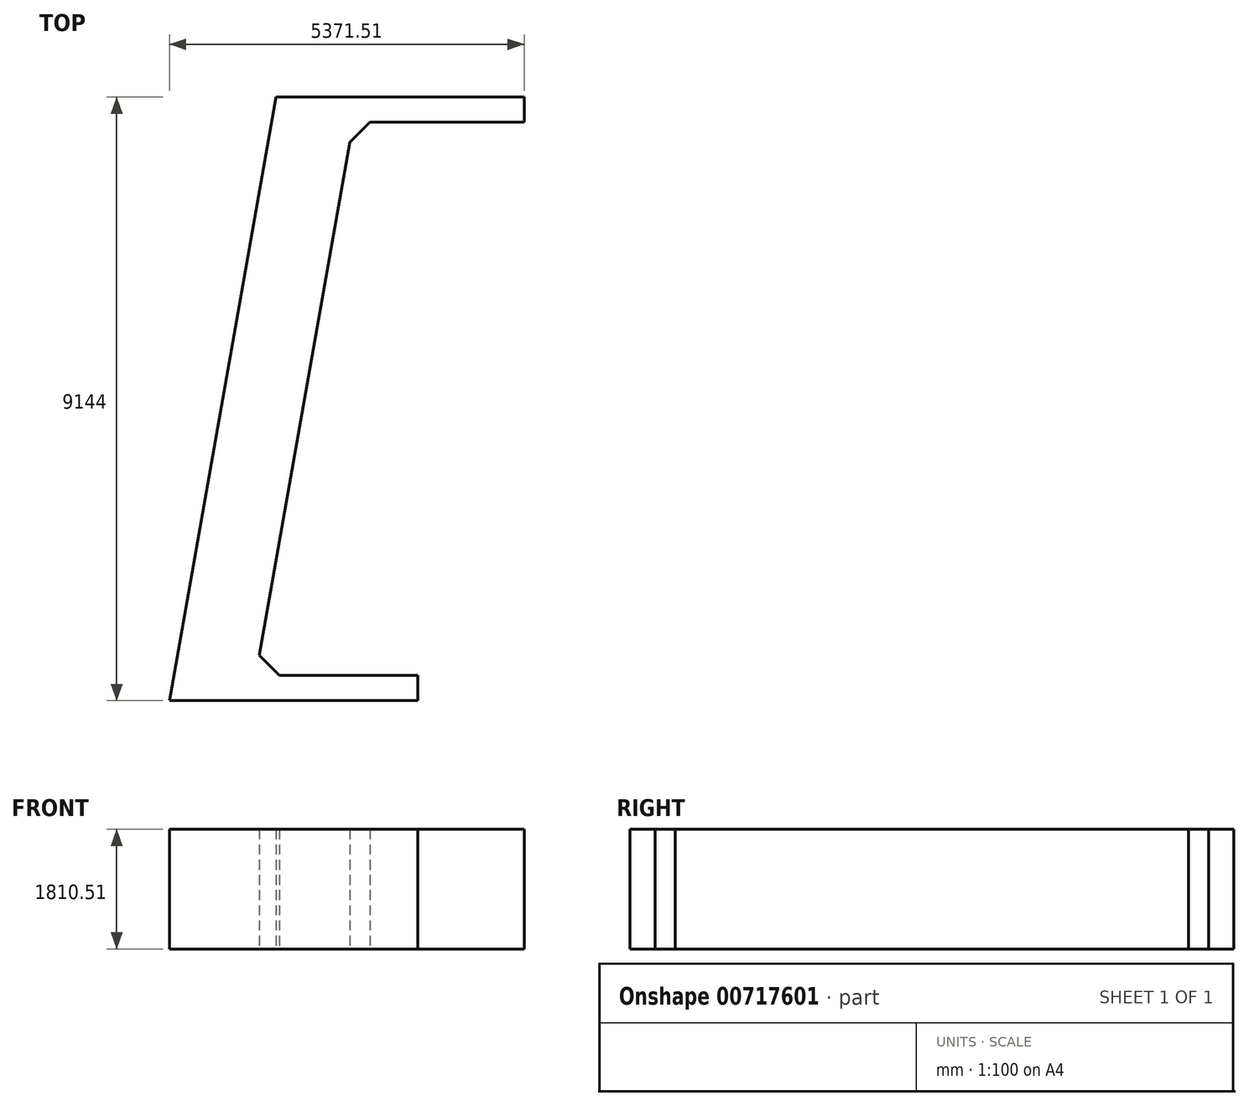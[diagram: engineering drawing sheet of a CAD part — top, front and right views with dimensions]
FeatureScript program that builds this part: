
annotation { "Feature Type Name" : "Feature", "Feature Type Description" : "" }
export const myFeature = defineFeature(function(context is Context, id is Id, definition is map)
    precondition{}
    {
        {
            var Q0;
            Q0=qCreatedBy(makeId("Top.planeOp"),FACE);
            var sketch = newSketch(context, id + "F0", { "sketchPlane" : qUnion([Q0])});
            skLineSegment(sketch, "E0", {"start": v(0, 0) * mm, "end": v(1612.33, 9144) * mm});
            skLineSegment(sketch, "E1", {"start": v(1612.33, 9144) * mm, "end": v(2729.93, 9144) * mm});
            skLineSegment(sketch, "E2", {"start": v(2729.93, 9144) * mm, "end": v(3034.73, 9144) * mm});
            skLineSegment(sketch, "E3", {"start": v(3034.73, 9144) * mm, "end": v(5371.51, 9144) * mm});
            skLineSegment(sketch, "E4", {"start": v(5371.51, 9144) * mm, "end": v(5371.51, 8763) * mm});
            skLineSegment(sketch, "E5", {"start": v(0, 0) * mm, "end": v(1358.9, 0) * mm});
            skLineSegment(sketch, "E6", {"start": v(1358.9, 0) * mm, "end": v(1663.7, 0) * mm});
            skLineSegment(sketch, "E7", {"start": v(1663.7, 0) * mm, "end": v(3759.2, 0) * mm});
            skLineSegment(sketch, "E8", {"start": v(3759.2, 0) * mm, "end": v(3759.2, 381) * mm});
            skLineSegment(sketch, "E9", {"start": v(5371.51, 8763) * mm, "end": v(3034.61, 8763) * mm});
            skLineSegment(sketch, "E10", {"start": v(3759.2, 381) * mm, "end": v(1663.7, 381) * mm});
            skLineSegment(sketch, "E11", {"start": v(1663.7, 381) * mm, "end": v(1358.9, 685.8) * mm});
            skLineSegment(sketch, "E12", {"start": v(3034.61, 8763) * mm, "end": v(2729.93, 8458.2) * mm});
            skLineSegment(sketch, "E13", {"start": v(1358.9, 685.8) * mm, "end": v(2729.93, 8458.2) * mm});
            skLineSegment(sketch, "E14", {"start": v(2231.34, 9144) * mm, "end": v(619, 0) * mm, "construction": true});
            skLineSegment(sketch, "E15", {"start": v(2684.34, 8199.75) * mm, "end": v(1445.84, 8199.75) * mm, "construction": true});
            skLineSegment(sketch, "E16", {"start": v(2257.46, 5779.77) * mm, "end": v(1019.13, 5779.77) * mm, "construction": true});
            skLineSegment(sketch, "E17", {"start": v(1830.58, 3359.78) * mm, "end": v(592.42, 3359.78) * mm, "construction": true});
            skLineSegment(sketch, "E18", {"start": v(1403.7, 939.8) * mm, "end": v(165.71, 939.8) * mm, "construction": true});
            skSolve(sketch);
        }
        {
            var Q0;
            Q0=makeQuery(id+"F0.imprint","IMPRINT",FACE,{"disambiguationData":[TD([[makeQuery(id+"F0.imprint","IMPRINT",EDGE,{"derivedFrom":sQuery(id+"F0.wireOp",EDGE,"E0")}),-1.0]])]});
            extrude(context, id + "F1", {"entities" : qUnion([Q0]), "depth" : 1810.5 * mm, "offsetDistance" : 30.48 * mm});
        }
    });
